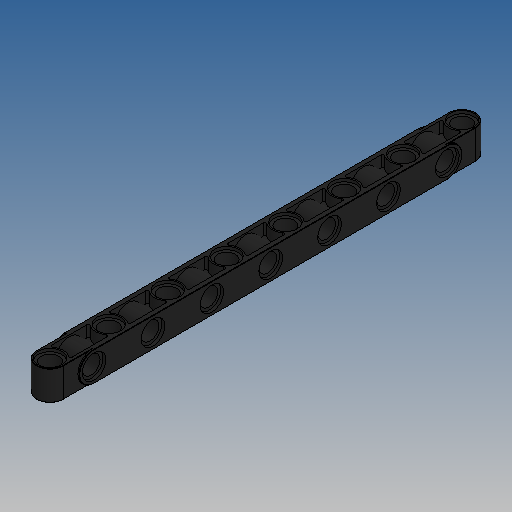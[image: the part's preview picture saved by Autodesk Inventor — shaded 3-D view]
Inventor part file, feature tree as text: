
AUTODESK INVENTOR PART (.ipt)
format: ipt  version: 2025 (Build 290162010, 162A)  size: 516,608 bytes
history: native  units: mm
features: sketch x8, extrude x7, mirror x3, fillet x2, delete_face x1, hole x1, pattern_linear x1
ambient origin geometry x8: Origin, YZ Plane, XZ Plane, XY Plane, X Axis, Y Axis, Z Axis, Center Point
bodies: Solid1 (feature_tree)
feature tree (23):
  extrude  "Extrusion1"  Depth=7.2mm
  sketch  "Sketch6"  dims[d48=112.0mm d49=6.4mm d50=4.8mm]
  extrude  "Extrusion7"  Depth=0.8mm TaperAngle=0.0deg
  extrude  "Extrusion8"  Depth=6.4mm
  mirror  "Mirror1"
  fillet  "Fillet2"  Radius=4.8mm
  mirror  "Spiegeln2"
  extrude  "Extrusion9"  Depth=0.8mm
  delete_face  "Fläche löschen1"
  fillet  "Rundung3"  Radius=70.0mm
  mirror  "Spiegeln3"
  extrude  "Extrusion10"  Depth=0.1mm
  extrude  "Extrusion11"  Depth=0.1mm
  extrude  "Extrusion12"  Depth=7.2mm TaperAngle=0.0deg
  hole  "Bohrung1"  [1 undecoded]
  pattern_linear  "Rechteckige Anordnung1"  Spacing1=0.0mm  [1 undecoded]
  sketch  "Sketch1"  dims[d14=8.0mm d15=0.0mm d32=7.2mm]
  sketch  "Skizze - Rechteckige Anordnung1"  dims[d41=0.8mm d42=0.0mm d43=3.1mm d44=0.0mm]
  sketch  "Skizze9"  dims[d51=16.0mm d52=0.8mm d53=70.0mm]
  sketch  "Skizze10"  dims[d55=16.0mm d56=10.0mm d58=10.0mm d60=0.4mm d61=0.1mm]
  sketch  "Skizze11"  dims[d63=0.4mm d64=0.0mm d65=0.1mm]
  sketch  "Skizze12"  dims[d66=7.2mm d67=0.4mm d68=0.0mm]
  sketch  "Skizze13"  dims[d69=6.4mm d70=0.8mm d71=0.0mm d72=0.8mm d73=0.0mm d74=4.8mm d75=40.0mm d76=4.0mm d77=2.0mm d78=90.0deg d79=8.0mm d80=20.594885mm d81=70.0mm d83=16.0mm d62=0.5mm]
note: 2 required parameter values undecoded (feature->parameter linkage not recoverable at this tier; creation-order binding heuristic only, values carry confidence <= 0.55)
